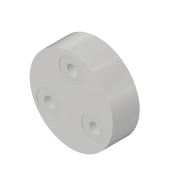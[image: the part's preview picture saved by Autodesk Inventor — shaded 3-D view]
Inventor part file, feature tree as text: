
AUTODESK INVENTOR PART (.ipt)
format: ipt  version: 2018 (Build 220112000, 112)  size: 119,808 bytes
history: native  units: in
note: dims shown in document units (in); Inventor stores cm internally (conversion verified against a paired STEP export)
features: extrude x4, sketch x4
ambient origin geometry x8: Origin, YZ Plane, XZ Plane, XY Plane, X Axis, Y Axis, Z Axis, Center Point
bodies: Solid1 (feature_tree)
feature tree (8):
  extrude  "Extrusion1"  Depth=3.5433in TaperAngle=360.0deg
  extrude  "Extrusion2"  Depth=0.0787in
  extrude  "Extrusion4"  Depth=2.38in
  extrude  "Extrusion5"  Depth=0.0591in TaperAngle=0.0deg
  sketch  "Sketch1"  dims[d0=3.5433in d1=0.0in d2=1.1811in d4=360.0deg]
  sketch  "Sketch2"  dims[d6=0.0787in d7=0.0in d10=8.0in]
  sketch  "Sketch5"  dims[d11=2.5in d12=2.38in]
  sketch  "Sketch6"  dims[d13=7.0in d14=0.0591in d15=0.0in d16=1.0in d17=1.1811in d19=360.0deg d21=2.1181in d22=0.0in]
